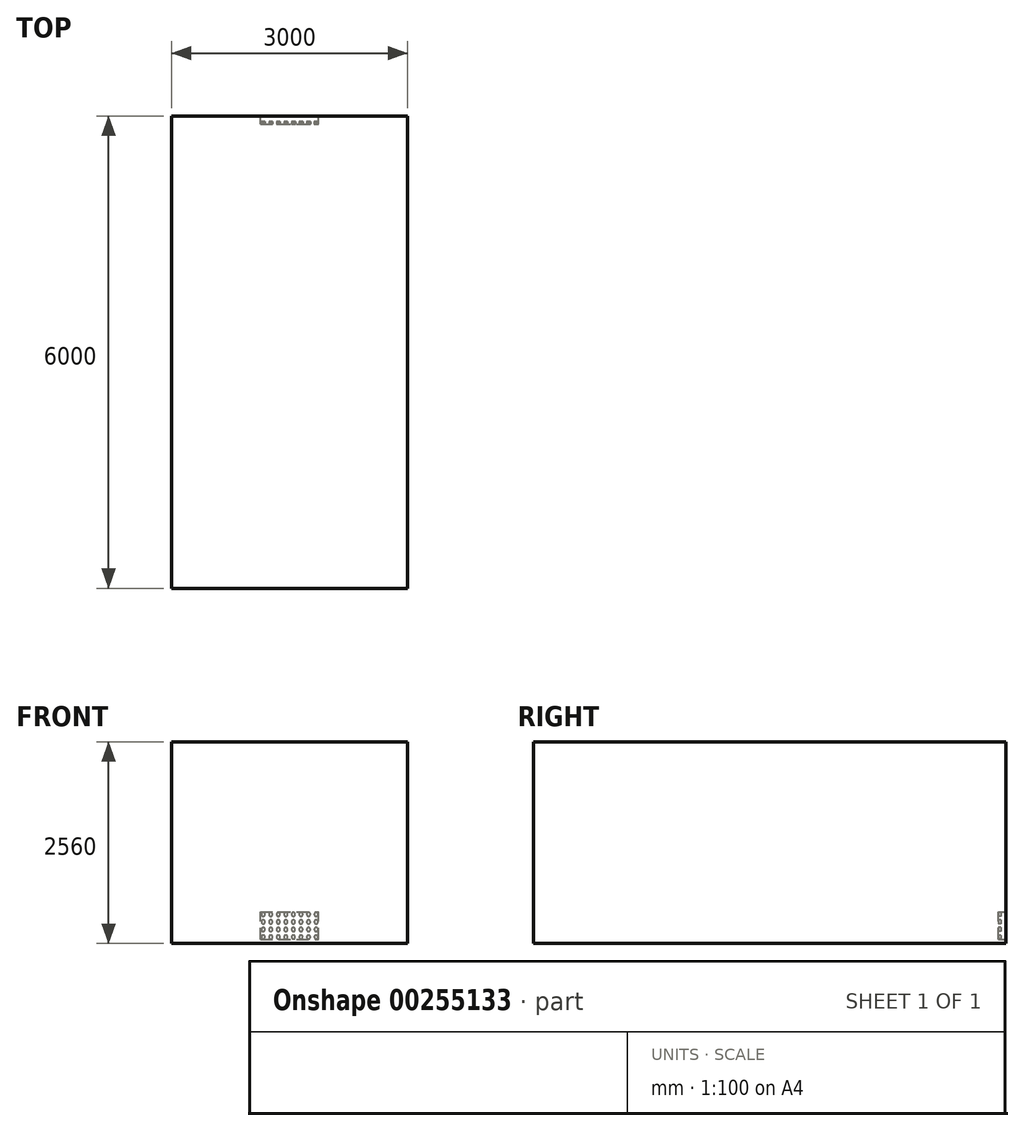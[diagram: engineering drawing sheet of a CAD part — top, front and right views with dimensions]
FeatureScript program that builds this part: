
annotation { "Feature Type Name" : "Feature", "Feature Type Description" : "" }
export const myFeature = defineFeature(function(context is Context, id is Id, definition is map)
    precondition{}
    {
        {
            var Q0;
            Q0=qCreatedBy(makeId("Front.planeOp"),FACE);
            var sketch = newSketch(context, id + "F0", { "sketchPlane" : qUnion([Q0])});
            skLineSegment(sketch, "E0.bottom", {"start": v(1500, -1280) * mm, "end": v(-1500, -1280) * mm});
            skLineSegment(sketch, "E0.top", {"start": v(1500, 1280) * mm, "end": v(-1500, 1280) * mm});
            skLineSegment(sketch, "E0.left", {"start": v(1500, -1280) * mm, "end": v(1500, 1280) * mm});
            skLineSegment(sketch, "E0.right", {"start": v(-1500, -1280) * mm, "end": v(-1500, 1280) * mm});
            skPoint(sketch, "E0.middle", {"position": v(0, 0) * mm});
            skSolve(sketch);
        }
        {
            var Q0;
            Q0 = qSketchRegion(id + "F0", true);
            extrude(context, id + "F1", {"entities" : qUnion([Q0]), "endBound" : BoundingType.SYMMETRIC, "depth" : 6000 * mm, "offsetDistance" : 25 * mm});
        }
        {
            var Q0;
            Q0=makeQuery(id+"F1.opExtrude","CAP_FACE",FACE,{"disambiguationData":[OSD([sQuery(id+"F0.wireOp",EDGE,"E0.bottom"),sQuery(id+"F0.wireOp",EDGE,"E0.top"),sQuery(id+"F0.wireOp",EDGE,"E0.left"),sQuery(id+"F0.wireOp",EDGE,"E0.right")])],"isStart":true});
            var sketch = newSketch(context, id + "F2", { "sketchPlane" : qUnion([Q0])});
            skLineSegment(sketch, "E1.bottom", {"start": v(750, -500) * mm, "end": v(-750, -500) * mm});
            skLineSegment(sketch, "E1.top", {"start": v(750, 1000) * mm, "end": v(-750, 1000) * mm});
            skLineSegment(sketch, "E1.left", {"start": v(750, -500) * mm, "end": v(750, 1000) * mm});
            skLineSegment(sketch, "E1.right", {"start": v(-750, -500) * mm, "end": v(-750, 1000) * mm});
            skPoint(sketch, "E1.middle", {"position": v(0, 250) * mm});
            skSolve(sketch);
        }
        {
            var Q0;
            Q0=makeQuery(id+"F2.imprint","IMPRINT",FACE,{"disambiguationData":[TD([[makeQuery(id+"F2.imprint","IMPRINT",EDGE,{"derivedFrom":sQuery(id+"F2.wireOp",EDGE,"E1.bottom")}),1.0]])]});
            var sketch = newSketch(context, id + "F3", { "sketchPlane" : qUnion([Q0])});
            skLineSegment(sketch, "E2.bottom", {"start": v(370, -1230) * mm, "end": v(-370, -1230) * mm});
            skLineSegment(sketch, "E2.top", {"start": v(370, -880) * mm, "end": v(-370, -880) * mm});
            skLineSegment(sketch, "E2.left", {"start": v(370, -1230) * mm, "end": v(370, -880) * mm});
            skLineSegment(sketch, "E2.right", {"start": v(-370, -1230) * mm, "end": v(-370, -880) * mm});
            skPoint(sketch, "E2.middle", {"position": v(0, -1055) * mm});
            skSolve(sketch);
        }
        {
            var Q0;
            Q0 = qSketchRegion(id + "F3", true);
            extrude(context, id + "F4", {"entities" : qUnion([Q0]), "operationType" : NewBodyOperationType.REMOVE, "oppositeDirection" : true, "depth" : 100 * mm, "offsetDistance" : 25 * mm});
        }
        {
            var Q0;
            Q0=makeQuery(id+"F4.boolean.opBoolean","COPY",FACE,{"derivedFrom":makeQuery(id+"F4.opExtrude","CAP_FACE",FACE,{"disambiguationData":[OSD([sQuery(id+"F3.wireOp",EDGE,"E2.bottom"),sQuery(id+"F3.wireOp",EDGE,"E2.top"),sQuery(id+"F3.wireOp",EDGE,"E2.left"),sQuery(id+"F3.wireOp",EDGE,"E2.right")])],"isStart":false})});
            var sketch = newSketch(context, id + "F5", { "sketchPlane" : qUnion([Q0])});
            skCircle(sketch, "E3", {"center": v(-336, -911) * mm, "radius": 24 * mm});
            skCircle(sketch, "E4.0.1.0", {"center": v(-336, -1007) * mm, "radius": 24 * mm});
            skCircle(sketch, "E4.0.2.0", {"center": v(-336, -1103) * mm, "radius": 24 * mm});
            skCircle(sketch, "E4.0.3.0", {"center": v(-336, -1199) * mm, "radius": 24 * mm});
            skCircle(sketch, "E4.1.0.0", {"center": v(-240, -911) * mm, "radius": 24 * mm});
            skCircle(sketch, "E4.1.1.0", {"center": v(-240, -1007) * mm, "radius": 24 * mm});
            skCircle(sketch, "E4.1.2.0", {"center": v(-240, -1103) * mm, "radius": 24 * mm});
            skCircle(sketch, "E4.1.3.0", {"center": v(-240, -1199) * mm, "radius": 24 * mm});
            skCircle(sketch, "E4.2.0.0", {"center": v(-144, -911) * mm, "radius": 24 * mm});
            skCircle(sketch, "E4.2.1.0", {"center": v(-144, -1007) * mm, "radius": 24 * mm});
            skCircle(sketch, "E4.2.2.0", {"center": v(-144, -1103) * mm, "radius": 24 * mm});
            skCircle(sketch, "E4.2.3.0", {"center": v(-144, -1199) * mm, "radius": 24 * mm});
            skCircle(sketch, "E4.3.0.0", {"center": v(-48, -911) * mm, "radius": 24 * mm});
            skCircle(sketch, "E4.3.1.0", {"center": v(-48, -1007) * mm, "radius": 24 * mm});
            skCircle(sketch, "E4.3.2.0", {"center": v(-48, -1103) * mm, "radius": 24 * mm});
            skCircle(sketch, "E4.3.3.0", {"center": v(-48, -1199) * mm, "radius": 24 * mm});
            skCircle(sketch, "E4.4.0.0", {"center": v(48, -911) * mm, "radius": 24 * mm});
            skCircle(sketch, "E4.4.1.0", {"center": v(48, -1007) * mm, "radius": 24 * mm});
            skCircle(sketch, "E4.4.2.0", {"center": v(48, -1103) * mm, "radius": 24 * mm});
            skCircle(sketch, "E4.4.3.0", {"center": v(48, -1199) * mm, "radius": 24 * mm});
            skCircle(sketch, "E4.5.0.0", {"center": v(144, -911) * mm, "radius": 24 * mm});
            skCircle(sketch, "E4.5.1.0", {"center": v(144, -1007) * mm, "radius": 24 * mm});
            skCircle(sketch, "E4.5.2.0", {"center": v(144, -1103) * mm, "radius": 24 * mm});
            skCircle(sketch, "E4.5.3.0", {"center": v(144, -1199) * mm, "radius": 24 * mm});
            skCircle(sketch, "E4.6.0.0", {"center": v(240, -911) * mm, "radius": 24 * mm});
            skCircle(sketch, "E4.6.1.0", {"center": v(240, -1007) * mm, "radius": 24 * mm});
            skCircle(sketch, "E4.6.2.0", {"center": v(240, -1103) * mm, "radius": 24 * mm});
            skCircle(sketch, "E4.6.3.0", {"center": v(240, -1199) * mm, "radius": 24 * mm});
            skCircle(sketch, "E4.7.0.0", {"center": v(336, -911) * mm, "radius": 24 * mm});
            skCircle(sketch, "E4.7.1.0", {"center": v(336, -1007) * mm, "radius": 24 * mm});
            skCircle(sketch, "E4.7.2.0", {"center": v(336, -1103) * mm, "radius": 24 * mm});
            skCircle(sketch, "E4.7.3.0", {"center": v(336, -1199) * mm, "radius": 24 * mm});
            skLineSegment(sketch, "E4.direction1", {"start": v(-336, -911) * mm, "end": v(-240, -911) * mm, "construction": true});
            skLineSegment(sketch, "E4.direction2", {"start": v(-336, -911) * mm, "end": v(-336, -1007) * mm, "construction": true});
            skSolve(sketch);
        }
        {
            var Q0;
            Q0 = qSketchRegion(id + "F5", true);
            extrude(context, id + "F6", {"entities" : qUnion([Q0]), "operationType" : NewBodyOperationType.ADD, "depth" : 32 * mm, "offsetDistance" : 25 * mm});
        }
    });
